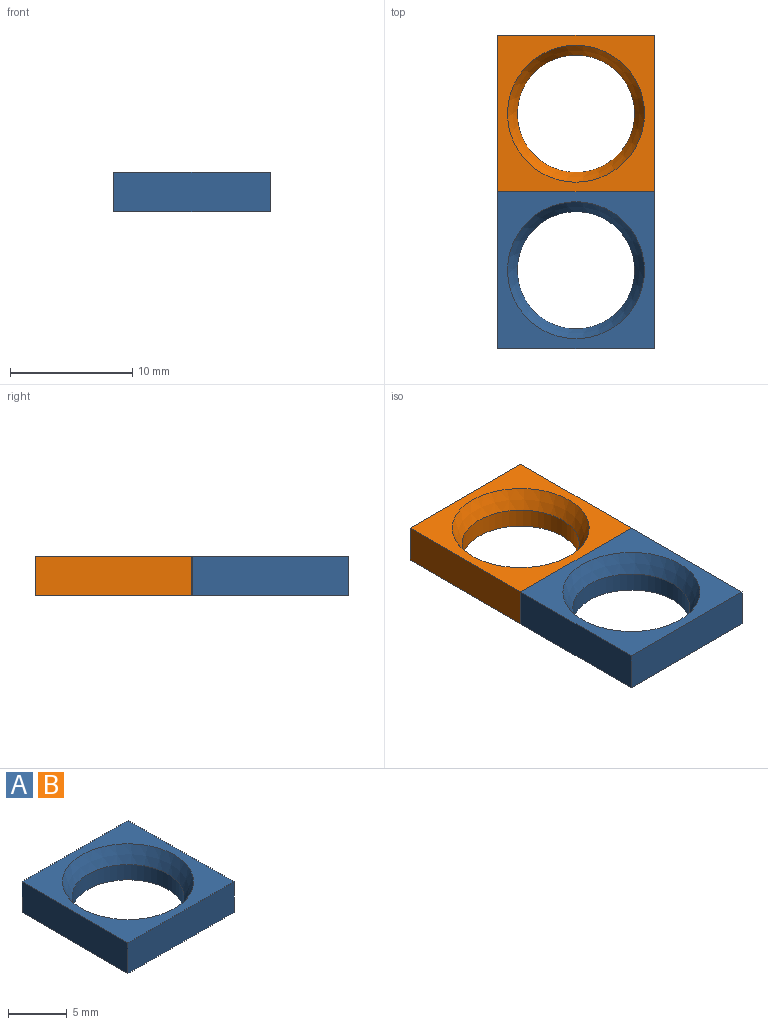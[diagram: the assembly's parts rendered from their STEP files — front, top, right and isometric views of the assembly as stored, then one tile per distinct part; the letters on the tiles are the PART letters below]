
ASSEMBLY  parts=2 mates=1
PART A: 8 faces, bbox 12.8x12.8x3.2 mm
  f0: plane 12.8x3.2mm, normal (1,0,0), area 41mm2, adj f1,f3,f5,f6
  f1: plane 12.8x3.2mm, normal (0,1,0), area 41mm2, adj f0,f2,f5,f6
  f2: plane 12.8x3.2mm, normal (-1,0,0), area 41mm2, adj f1,f3,f5,f6
  f3: plane 12.8x3.2mm, normal (0,-1,0), area 41mm2, adj f0,f2,f5,f6
  f4: cylinder r=4.8mm len=9.6mm, axis (0,0,-1), area 48.3mm2, adj f6,f7
  f5: plane 12.8x12.8mm, normal (0,0,1), area 65.3mm2, adj f0,f1,f2,f3,f7
  f6: plane 12.8x12.8mm, normal (0,0,-1), area 91.5mm2, adj f0,f1,f2,f3,f4
  f7: cone r=4.8mm half-angle=26.6deg, axis (0,0,1), area 58.4mm2, adj f4,f5
PART B: same geometry as A
PLACE A t=(4.08,-16.86,7.44)mm
PLACE B t=(4.08,-4.06,7.44)mm
MATE fastened B.f3 <-> A.f1  axis (0,-1,0) through (-11.92,5.54,9.04)mm
